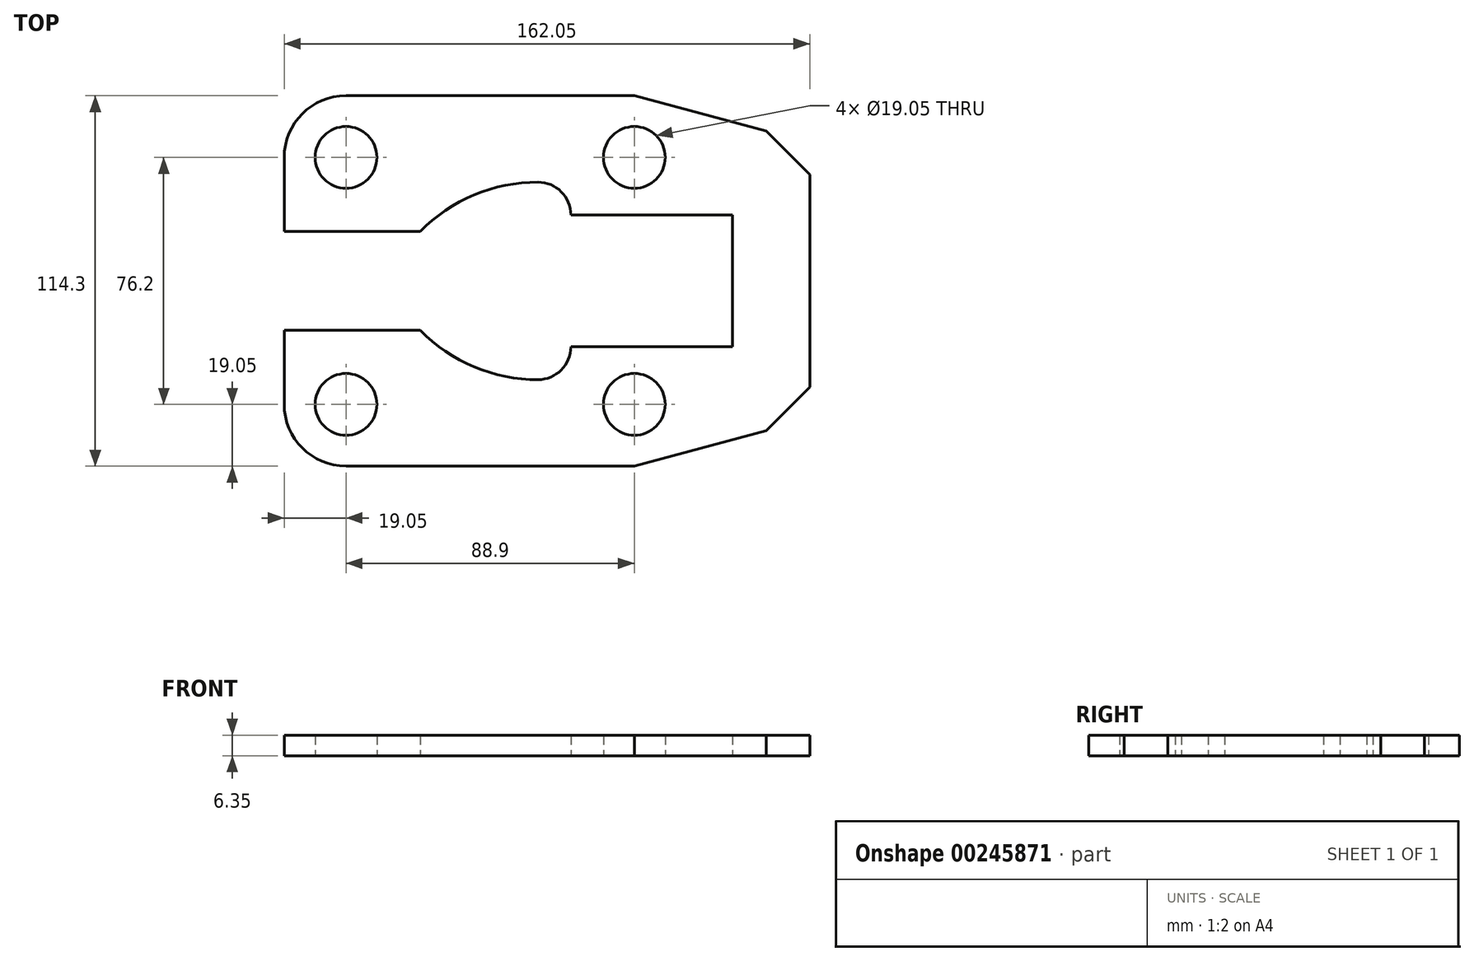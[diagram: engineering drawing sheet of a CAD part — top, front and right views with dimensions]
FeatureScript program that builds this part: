
annotation { "Feature Type Name" : "Feature", "Feature Type Description" : "" }
export const myFeature = defineFeature(function(context is Context, id is Id, definition is map)
    precondition{}
    {
        {
            var Q0;
            Q0=qCreatedBy(makeId("Top.planeOp"),FACE);
            var sketch = newSketch(context, id + "F0", { "sketchPlane" : qUnion([Q0])});
            skCircle(sketch, "E0", {"center": v(-54.33, 38.1) * mm, "radius": 9.53 * mm});
            skArc(sketch, "E1", {"start": v(-54.33, 57.15) * mm, "mid": v(-67.8, 51.57) * mm, "end": v(-73.38, 38.1) * mm});
            skLineSegment(sketch, "E2", {"start": v(-54.33, 38.1) * mm, "end": v(-85.2, 38.1) * mm, "construction": true});
            skLineSegment(sketch, "E3", {"start": v(-54.33, 38.1) * mm, "end": v(-54.33, 67.54) * mm, "construction": true});
            skLineSegment(sketch, "E4", {"start": v(-54.33, 57.15) * mm, "end": v(34.57, 57.15) * mm});
            skLineSegment(sketch, "E5", {"start": v(-73.38, 38.1) * mm, "end": v(-73.38, 15.24) * mm});
            skPoint(sketch, "E6.orphan", {"position": v(-73.38, 0) * mm});
            skLineSegment(sketch, "E7", {"start": v(34.57, 57.15) * mm, "end": v(75.21, 46.26) * mm});
            skLineSegment(sketch, "E8", {"start": v(75.21, 46.26) * mm, "end": v(88.67, 32.8) * mm});
            skLineSegment(sketch, "E9", {"start": v(88.67, 32.8) * mm, "end": v(88.67, 0) * mm});
            skCircle(sketch, "E10", {"center": v(34.57, 38.1) * mm, "radius": 9.53 * mm});
            skArc(sketch, "E11", {"start": v(15.01, 20.32) * mm, "mid": v(12.04, 27.5) * mm, "end": v(4.85, 30.48) * mm});
            skLineSegment(sketch, "E12", {"start": v(15.01, 20.32) * mm, "end": v(64.8, 20.32) * mm});
            skLineSegment(sketch, "E13", {"start": v(-73.38, 15.24) * mm, "end": v(-31.43, 15.24) * mm});
            skLineSegment(sketch, "E14", {"start": v(64.8, 20.32) * mm, "end": v(64.8, 0) * mm});
            skArc(sketch, "E15.MirrorCS", {"start": v(-54.33, -57.15) * mm, "mid": v(-67.8, -51.57) * mm, "end": v(-73.38, -38.1) * mm});
            skCircle(sketch, "E16.MirrorC", {"center": v(-54.33, -38.1) * mm, "radius": 9.53 * mm});
            skLineSegment(sketch, "E17.MirrorCS", {"start": v(-54.33, -57.15) * mm, "end": v(34.57, -57.15) * mm});
            skLineSegment(sketch, "E18.MirrorCS", {"start": v(-73.38, -38.1) * mm, "end": v(-73.38, -15.24) * mm});
            skCircle(sketch, "E19.MirrorC", {"center": v(34.57, -38.1) * mm, "radius": 9.53 * mm});
            skLineSegment(sketch, "E20.MirrorCS", {"start": v(34.57, -57.15) * mm, "end": v(75.21, -46.26) * mm});
            skLineSegment(sketch, "E21.MirrorCS", {"start": v(88.67, -32.8) * mm, "end": v(88.67, 0) * mm});
            skArc(sketch, "E22.MirrorC", {"start": v(15.01, -20.32) * mm, "mid": v(12.04, -27.5) * mm, "end": v(4.85, -30.48) * mm});
            skLineSegment(sketch, "E23.MirrorCS", {"start": v(75.21, -46.26) * mm, "end": v(88.67, -32.8) * mm});
            skLineSegment(sketch, "E24.MirrorCS", {"start": v(64.8, -20.32) * mm, "end": v(64.8, 0) * mm});
            skLineSegment(sketch, "E25.MirrorCS", {"start": v(-73.38, -15.24) * mm, "end": v(-31.43, -15.24) * mm});
            skLineSegment(sketch, "E26.MirrorCS", {"start": v(15.01, -20.32) * mm, "end": v(64.8, -20.32) * mm});
            skArc(sketch, "E27.trimOffspring", {"start": v(4.85, 30.48) * mm, "mid": v(-14.82, 26.52) * mm, "end": v(-31.43, 15.24) * mm});
            skArc(sketch, "E28.trimOffspring", {"start": v(-31.43, -15.24) * mm, "mid": v(-14.82, -26.52) * mm, "end": v(4.85, -30.48) * mm});
            skPoint(sketch, "E29.orphan", {"position": v(-3.95, 15.24) * mm});
            skPoint(sketch, "E30.orphan", {"position": v(-3.95, -15.24) * mm});
            skPoint(sketch, "E31.orphan", {"position": v(70.96, 57.15) * mm});
            skPoint(sketch, "E32.orphan", {"position": v(88.67, -20.32) * mm});
            skPoint(sketch, "E33.orphan", {"position": v(88.67, 20.32) * mm});
            skSolve(sketch);
        }
        {
            var Q0;
            Q0 = qSketchRegion(id + "F0", true);
            extrude(context, id + "F1", {"entities" : qUnion([Q0]), "depth" : 6.35 * mm});
        }
    });
